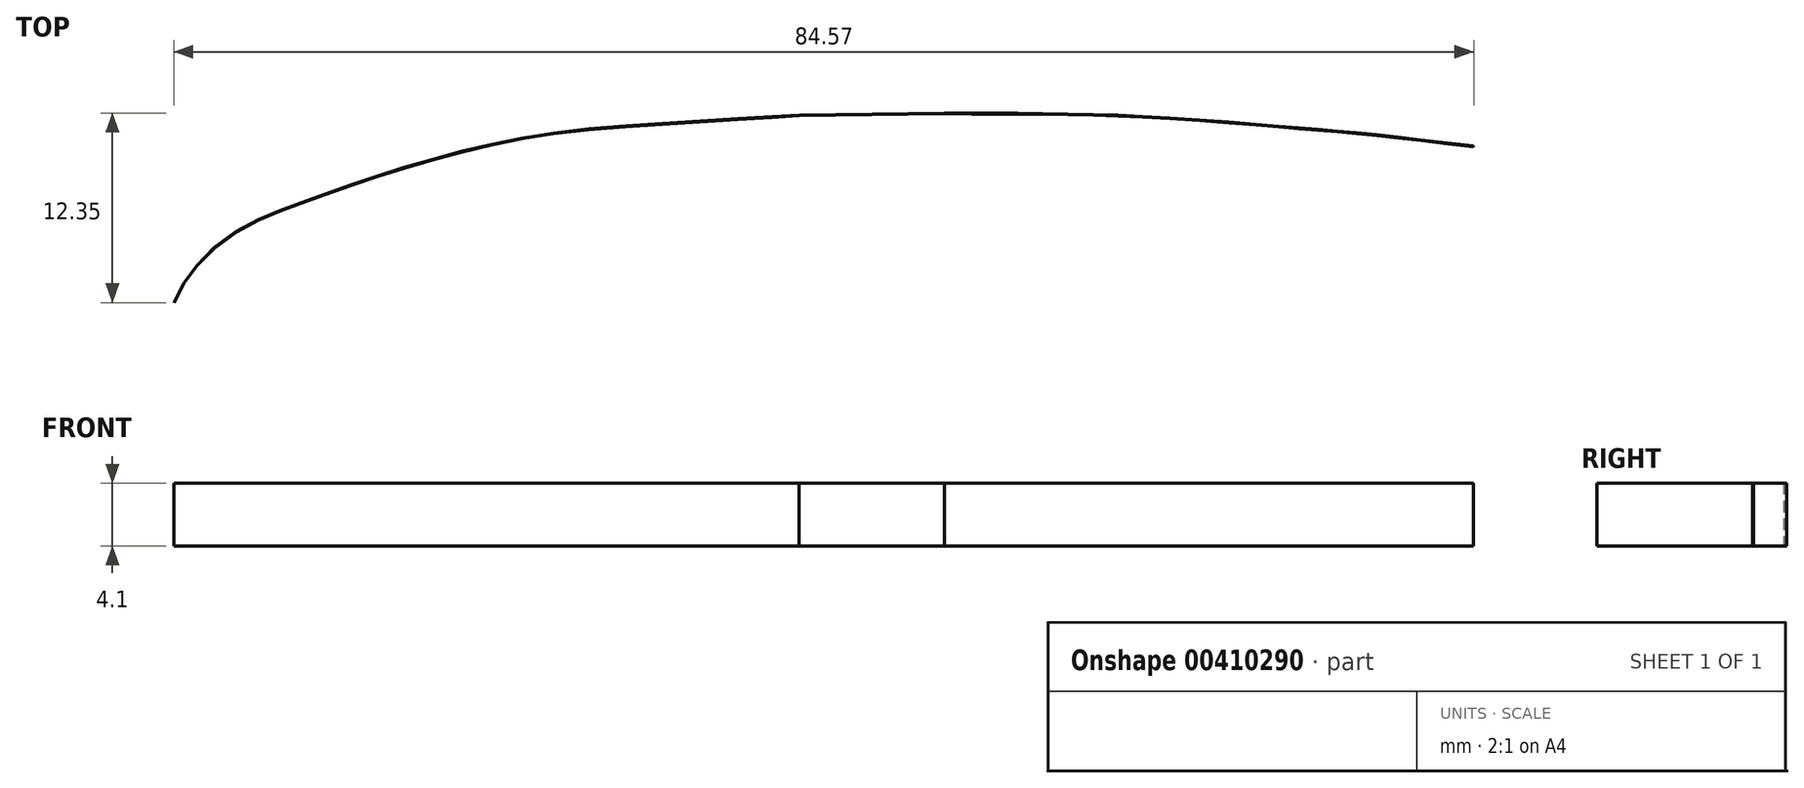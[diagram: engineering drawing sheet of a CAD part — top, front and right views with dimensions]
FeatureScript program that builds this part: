
annotation { "Feature Type Name" : "Feature", "Feature Type Description" : "" }
export const myFeature = defineFeature(function(context is Context, id is Id, definition is map)
    precondition{}
    {
        {
            var Q0;
            Q0=qCreatedBy(makeId("Top.planeOp"),FACE);
            var sketch = newSketch(context, id + "F0", { "sketchPlane" : qUnion([Q0])});
            skLineSegment(sketch, "E0", {"start": v(-49.1, -7.29) * mm, "end": v(-49.1, 15.91) * mm, "construction": true});
            skLineSegment(sketch, "E1", {"start": v(56.1, -3.3) * mm, "end": v(55.68, 15.32) * mm, "construction": true});
            skFitSpline(sketch, "E2.0", {"points": [v(-7.16, 11.34) * mm, v(-8.7, 11.24) * mm, v(-11.02, 11.1) * mm, v(-14.06, 10.9) * mm, v(-17.04, 10.72) * mm, v(-19.9, 10.52) * mm, v(-22.68, 10.23) * mm, v(-24.74, 9.92) * mm, v(-26.8, 9.52) * mm, v(-28.8, 9.06) * mm, v(-30.7, 8.56) * mm, v(-32.46, 8.05) * mm, v(-34.1, 7.54) * mm, v(-35.64, 7.03) * mm, v(-37.16, 6.5) * mm, v(-38.65, 5.98) * mm, v(-39.87, 5.53) * mm, v(-40.85, 5.16) * mm, v(-41.8, 4.78) * mm, v(-42.94, 4.26) * mm, v(-44.23, 3.5) * mm, v(-45.45, 2.52) * mm, v(-46.35, 1.6) * mm, v(-46.94, 0.82) * mm, v(-47.45, 0.03) * mm, v(-47.92, -0.97) * mm, v(-48.28, -2.27) * mm, v(-48.48, -3.72) * mm, v(-48.48, -4.98) * mm, v(-48.37, -6) * mm, v(-48.22, -6.76) * mm, v(-48, -7.52) * mm, v(-47.64, -8.53) * mm, v(-47.03, -9.76) * mm, v(-46.16, -11.04) * mm, v(-45.39, -11.86) * mm, v(-44.73, -12.42) * mm, v(-44.23, -12.82) * mm, v(-43.7, -13.19) * mm, v(-42.97, -13.66) * mm, v(-42.25, -14.07) * mm, v(-41.5, -14.41) * mm, v(-40.9, -14.62) * mm, v(-40.26, -14.8) * mm, v(-39.57, -14.92) * mm, v(-38.86, -14.99) * mm, v(-38.15, -15) * mm, v(-37.45, -14.98) * mm, v(-36.8, -14.88) * mm, v(-36.13, -14.74) * mm, v(-35.25, -14.49) * mm, v(-34.35, -14.16) * mm, v(-33.37, -13.82) * mm, v(-32.36, -13.48) * mm, v(-31.03, -13.06) * mm, v(-29.3, -12.61) * mm, v(-27.44, -12.24) * mm, v(-25.89, -12) * mm, v(-24.73, -11.82) * mm, v(-23.93, -11.7) * mm, v(-23.2, -11.58) * mm, v(-22.55, -11.46) * mm, v(-21.9, -11.35) * mm, v(-21.24, -11.25) * mm, v(-20.54, -11.16) * mm, v(-19.75, -11.07) * mm, v(-18.91, -11) * mm, v(-18.02, -10.93) * mm, v(-17.1, -10.87) * mm, v(-16.19, -10.82) * mm, v(-15.27, -10.79) * mm, v(-14.39, -10.76) * mm, v(-13.53, -10.75) * mm, v(-12.4, -10.76) * mm, v(-11.27, -10.79) * mm, v(-10.13, -10.85) * mm, v(-8.95, -10.94) * mm, v(-7.77, -11.05) * mm, v(-6.62, -11.18) * mm, v(-5.79, -11.27) * mm, v(-5, -11.36) * mm, v(-4.02, -11.47) * mm, v(-2.87, -11.6) * mm, v(-1.47, -11.7) * mm, v(0.14, -11.8) * mm, v(1.9, -11.88) * mm, v(3.11, -11.93) * mm, v(3.72, -11.95) * mm]});
            skFitSpline(sketch, "E2.1", {"points": [v(-7.21, 11.34) * mm, v(-4.05, 11.38) * mm, v(-0.89, 11.42) * mm, v(2.27, 11.46) * mm]});
            skFitSpline(sketch, "E2.2", {"points": [v(3.5, -11.97) * mm, v(4.13, -11.85) * mm, v(5.02, -11.8) * mm, v(6.1, -11.8) * mm, v(6.78, -11.8) * mm, v(7.33, -11.78) * mm, v(7.9, -11.75) * mm, v(8.66, -11.67) * mm, v(9.64, -11.54) * mm, v(10.65, -11.39) * mm, v(11.68, -11.2) * mm, v(13.05, -10.96) * mm, v(14.68, -10.67) * mm, v(16.31, -10.31) * mm, v(17.67, -9.95) * mm, v(18.73, -9.63) * mm, v(19.84, -9.26) * mm, v(20.96, -8.86) * mm, v(22.04, -8.45) * mm, v(23.06, -8.05) * mm, v(23.82, -7.74) * mm, v(24.36, -7.52) * mm, v(24.85, -7.31) * mm, v(25.4, -7.09) * mm, v(26.03, -6.86) * mm, v(26.7, -6.7) * mm, v(27.43, -6.6) * mm, v(28.16, -6.58) * mm, v(29.14, -6.62) * mm, v(30.06, -6.75) * mm, v(30.96, -6.99) * mm, v(31.86, -7.3) * mm, v(33.02, -7.83) * mm, v(34.24, -8.6) * mm, v(35.27, -9.38) * mm, v(36.04, -10.03) * mm, v(36.63, -10.6) * mm, v(37.06, -11.08) * mm, v(37.36, -11.44) * mm, v(37.63, -11.81) * mm, v(37.86, -12.2) * mm, v(38.04, -12.56) * mm, v(38.18, -12.89) * mm, v(38.3, -13.18) * mm, v(38.4, -13.42) * mm, v(38.5, -13.62) * mm, v(38.58, -13.76) * mm, v(38.65, -13.86) * mm, v(38.74, -13.97) * mm, v(38.87, -14.1) * mm, v(39.06, -14.28) * mm, v(39.35, -14.49) * mm, v(39.67, -14.68) * mm, v(40, -14.82) * mm, v(40.33, -14.93) * mm, v(40.73, -15.01) * mm, v(41.27, -15.03) * mm, v(41.9, -14.95) * mm, v(42.66, -14.76) * mm, v(43.56, -14.46) * mm, v(44.54, -14.08) * mm, v(45.57, -13.66) * mm, v(46.63, -13.22) * mm, v(47.52, -12.87) * mm, v(48.21, -12.61) * mm, v(48.89, -12.38) * mm, v(49.67, -12.12) * mm, v(50.52, -11.83) * mm, v(51.28, -11.52) * mm, v(51.84, -11.22) * mm, v(52.25, -10.94) * mm, v(52.65, -10.62) * mm, v(53.13, -10.13) * mm, v(53.66, -9.45) * mm, v(54.13, -8.69) * mm, v(54.44, -8.02) * mm, v(54.64, -7.48) * mm, v(54.81, -6.94) * mm, v(54.96, -6.25) * mm, v(55.06, -5.42) * mm, v(55.1, -4.58) * mm, v(55.1, -3.75) * mm, v(55.1, -2.92) * mm, v(55.05, -1.92) * mm, v(54.94, -1.02) * mm, v(54.7, -0.16) * mm, v(54.41, 0.5) * mm, v(54.05, 1.2) * mm, v(53.47, 2.12) * mm, v(52.63, 3.23) * mm, v(51.72, 4.23) * mm, v(51, 4.94) * mm, v(50.47, 5.43) * mm, v(49.97, 5.86) * mm, v(49.48, 6.25) * mm, v(48.96, 6.6) * mm, v(48.37, 6.96) * mm, v(47.68, 7.3) * mm, v(46.7, 7.73) * mm, v(45.37, 8.19) * mm, v(44.14, 8.44) * mm, v(43.04, 8.6) * mm, v(42.12, 8.7) * mm, v(41.07, 8.8) * mm, v(39.88, 8.94) * mm, v(38.56, 9.09) * mm, v(36.7, 9.31) * mm, v(34.75, 9.54) * mm, v(32.85, 9.77) * mm, v(31.48, 9.92) * mm, v(30.22, 10.06) * mm, v(29.07, 10.17) * mm, v(28, 10.27) * mm, v(26.96, 10.36) * mm, v(25.92, 10.45) * mm, v(24.85, 10.53) * mm, v(23.72, 10.63) * mm, v(22.1, 10.77) * mm, v(19.87, 10.95) * mm, v(17.38, 11.12) * mm, v(15.24, 11.24) * mm, v(13.55, 11.31) * mm, v(11.79, 11.37) * mm, v(9.97, 11.4) * mm, v(8.2, 11.43) * mm, v(6.5, 11.45) * mm, v(5, 11.45) * mm, v(3.72, 11.45) * mm, v(2.92, 11.46) * mm, v(2.47, 11.46) * mm, v(2.3, 11.46) * mm, v(2.24, 11.46) * mm]});
            skArc(sketch, "E3", {"start": v(9.18, 8.55) * mm, "mid": v(8.26, 9.24) * mm, "end": v(7.1, 9.31) * mm});
            skArc(sketch, "E4", {"start": v(36.35, 6.78) * mm, "mid": v(35.45, 7.49) * mm, "end": v(34.3, 7.58) * mm});
            skFitSpline(sketch, "E5.0", {"points": [v(-7.18, 11.29) * mm, v(-8.73, 11.2) * mm, v(-11.04, 11.05) * mm, v(-14.07, 10.86) * mm, v(-17.06, 10.67) * mm, v(-19.92, 10.47) * mm, v(-22.7, 10.18) * mm, v(-24.75, 9.87) * mm, v(-26.81, 9.47) * mm, v(-28.81, 9.01) * mm, v(-30.72, 8.5) * mm, v(-32.48, 8) * mm, v(-34.11, 7.5) * mm, v(-35.66, 6.98) * mm, v(-37.18, 6.46) * mm, v(-38.67, 5.93) * mm, v(-39.9, 5.48) * mm, v(-40.87, 5.12) * mm, v(-41.82, 4.74) * mm, v(-42.96, 4.21) * mm, v(-44.25, 3.45) * mm, v(-45.47, 2.47) * mm, v(-46.37, 1.54) * mm, v(-46.96, 0.77) * mm, v(-47.47, -0.02) * mm, v(-47.94, -1.02) * mm, v(-48.3, -2.32) * mm, v(-48.5, -3.76) * mm, v(-48.5, -5.02) * mm, v(-48.39, -6.05) * mm, v(-48.24, -6.8) * mm, v(-48.03, -7.57) * mm, v(-47.65, -8.58) * mm, v(-47.05, -9.8) * mm, v(-46.17, -11.09) * mm, v(-45.4, -11.9) * mm, v(-44.75, -12.47) * mm, v(-44.25, -12.87) * mm, v(-43.72, -13.24) * mm, v(-43, -13.71) * mm, v(-42.27, -14.12) * mm, v(-41.52, -14.46) * mm, v(-40.92, -14.67) * mm, v(-40.28, -14.84) * mm, v(-39.59, -14.97) * mm, v(-38.88, -15.04) * mm, v(-38.17, -15.06) * mm, v(-37.47, -15.02) * mm, v(-36.8, -14.93) * mm, v(-36.15, -14.79) * mm, v(-35.27, -14.54) * mm, v(-34.36, -14.21) * mm, v(-33.39, -13.87) * mm, v(-32.38, -13.53) * mm, v(-31.05, -13.11) * mm, v(-29.33, -12.66) * mm, v(-27.46, -12.3) * mm, v(-25.9, -12.04) * mm, v(-24.75, -11.87) * mm, v(-23.94, -11.74) * mm, v(-23.23, -11.62) * mm, v(-22.56, -11.51) * mm, v(-21.92, -11.4) * mm, v(-21.26, -11.3) * mm, v(-20.56, -11.2) * mm, v(-19.77, -11.12) * mm, v(-18.93, -11.04) * mm, v(-18.04, -10.97) * mm, v(-17.13, -10.92) * mm, v(-16.2, -10.87) * mm, v(-15.3, -10.84) * mm, v(-14.4, -10.81) * mm, v(-13.55, -10.8) * mm, v(-12.41, -10.8) * mm, v(-11.3, -10.84) * mm, v(-10.15, -10.9) * mm, v(-8.97, -10.99) * mm, v(-7.79, -11.1) * mm, v(-6.64, -11.23) * mm, v(-5.8, -11.32) * mm, v(-5.02, -11.4) * mm, v(-4.04, -11.52) * mm, v(-2.9, -11.64) * mm, v(-1.49, -11.76) * mm, v(0.12, -11.85) * mm, v(1.88, -11.93) * mm, v(3.1, -11.98) * mm, v(3.7, -12) * mm]});
            skFitSpline(sketch, "E5.1", {"points": [v(-7.23, 11.29) * mm, v(-4.07, 11.33) * mm, v(-0.9, 11.37) * mm, v(2.26, 11.41) * mm]});
            skFitSpline(sketch, "E5.2", {"points": [v(3.48, -12.02) * mm, v(4.11, -11.9) * mm, v(5, -11.85) * mm, v(6.09, -11.85) * mm, v(6.76, -11.85) * mm, v(7.3, -11.83) * mm, v(7.88, -11.8) * mm, v(8.65, -11.72) * mm, v(9.62, -11.6) * mm, v(10.63, -11.43) * mm, v(11.66, -11.26) * mm, v(13.03, -11.01) * mm, v(14.67, -10.72) * mm, v(16.3, -10.36) * mm, v(17.65, -10) * mm, v(18.7, -9.68) * mm, v(19.82, -9.3) * mm, v(20.94, -8.9) * mm, v(22.02, -8.5) * mm, v(23.04, -8.1) * mm, v(23.8, -7.79) * mm, v(24.34, -7.57) * mm, v(24.83, -7.36) * mm, v(25.37, -7.14) * mm, v(26.01, -6.91) * mm, v(26.69, -6.74) * mm, v(27.41, -6.65) * mm, v(28.14, -6.63) * mm, v(29.12, -6.67) * mm, v(30.04, -6.8) * mm, v(30.94, -7.04) * mm, v(31.84, -7.35) * mm, v(33, -7.88) * mm, v(34.22, -8.65) * mm, v(35.25, -9.43) * mm, v(36.02, -10.08) * mm, v(36.61, -10.65) * mm, v(37.04, -11.13) * mm, v(37.34, -11.5) * mm, v(37.61, -11.86) * mm, v(37.84, -12.25) * mm, v(38.02, -12.6) * mm, v(38.16, -12.94) * mm, v(38.28, -13.22) * mm, v(38.38, -13.47) * mm, v(38.48, -13.67) * mm, v(38.56, -13.8) * mm, v(38.63, -13.9) * mm, v(38.72, -14.02) * mm, v(38.85, -14.16) * mm, v(39.04, -14.33) * mm, v(39.33, -14.54) * mm, v(39.65, -14.73) * mm, v(39.98, -14.87) * mm, v(40.3, -14.98) * mm, v(40.71, -15.06) * mm, v(41.25, -15.08) * mm, v(41.88, -15) * mm, v(42.64, -14.81) * mm, v(43.54, -14.51) * mm, v(44.52, -14.13) * mm, v(45.55, -13.71) * mm, v(46.62, -13.27) * mm, v(47.5, -12.92) * mm, v(48.2, -12.66) * mm, v(48.87, -12.43) * mm, v(49.65, -12.17) * mm, v(50.5, -11.88) * mm, v(51.26, -11.57) * mm, v(51.82, -11.27) * mm, v(52.23, -10.99) * mm, v(52.63, -10.67) * mm, v(53.11, -10.18) * mm, v(53.64, -9.5) * mm, v(54.1, -8.74) * mm, v(54.42, -8.07) * mm, v(54.63, -7.53) * mm, v(54.8, -6.99) * mm, v(54.94, -6.3) * mm, v(55.04, -5.47) * mm, v(55.09, -4.63) * mm, v(55.09, -3.8) * mm, v(55.07, -2.97) * mm, v(55.04, -1.97) * mm, v(54.92, -1.07) * mm, v(54.67, -0.21) * mm, v(54.4, 0.46) * mm, v(54.03, 1.15) * mm, v(53.45, 2.07) * mm, v(52.6, 3.18) * mm, v(51.7, 4.18) * mm, v(50.98, 4.89) * mm, v(50.45, 5.38) * mm, v(49.95, 5.82) * mm, v(49.46, 6.2) * mm, v(48.94, 6.56) * mm, v(48.35, 6.9) * mm, v(47.66, 7.25) * mm, v(46.67, 7.68) * mm, v(45.35, 8.14) * mm, v(44.12, 8.4) * mm, v(43.02, 8.55) * mm, v(42.1, 8.65) * mm, v(41.06, 8.76) * mm, v(39.86, 8.89) * mm, v(38.54, 9.04) * mm, v(36.68, 9.26) * mm, v(34.73, 9.5) * mm, v(32.83, 9.72) * mm, v(31.46, 9.87) * mm, v(30.2, 10) * mm, v(29.06, 10.12) * mm, v(27.98, 10.22) * mm, v(26.94, 10.31) * mm, v(25.9, 10.4) * mm, v(24.84, 10.48) * mm, v(23.7, 10.58) * mm, v(22.08, 10.72) * mm, v(19.85, 10.9) * mm, v(17.36, 11.07) * mm, v(15.22, 11.19) * mm, v(13.53, 11.26) * mm, v(11.77, 11.32) * mm, v(9.96, 11.36) * mm, v(8.17, 11.38) * mm, v(6.49, 11.4) * mm, v(4.97, 11.4) * mm, v(3.7, 11.4) * mm, v(2.9, 11.4) * mm, v(2.45, 11.4) * mm, v(2.29, 11.41) * mm, v(2.22, 11.41) * mm]});
            skCircle(sketch, "E6", {"center": v(-44.34, -5.92) * mm, "radius": 2.1 * mm});
            skCircle(sketch, "E7", {"center": v(-19.07, 6.55) * mm, "radius": 2.1 * mm});
            skArc(sketch, "E8", {"start": v(9.14, 8.55) * mm, "mid": v(8.25, 9.21) * mm, "end": v(7.15, 9.3) * mm});
            skArc(sketch, "E9", {"start": v(9.14, 8.55) * mm, "mid": v(9.22, 8.59) * mm, "end": v(9.3, 8.63) * mm});
            skFitSpline(sketch, "E10", {"points": [v(-15.32, 8.96) * mm, v(7.15, 9.3) * mm, v(17.25, 3.77) * mm], "startDerivative": vector(42.73, 4.67) * mm, "endDerivative": vector(21.23, -16.2) * mm});
            skFitSpline(sketch, "E11.trimOffspring", {"points": [v(-15.32, 8.96) * mm, v(7.15, 9.3) * mm, v(17.25, 3.77) * mm], "startDerivative": vector(42.73, 4.67) * mm, "endDerivative": vector(21.23, -16.2) * mm});
            skArc(sketch, "E12.trimOffspring", {"start": v(-21.7, 4.94) * mm, "mid": v(-33.14, 5.53) * mm, "end": v(-42.33, -1.34) * mm});
            skArc(sketch, "E13", {"start": v(-21.7, 4.94) * mm, "mid": v(-20.44, 4.08) * mm, "end": v(-18.95, 3.77) * mm});
            skFitSpline(sketch, "E14", {"points": [v(-15.32, 8.96) * mm, v(-16.43, 8.6) * mm], "startDerivative": vector(-1.12, -0.35) * mm, "endDerivative": vector(-1.12, -0.35) * mm});
            skArc(sketch, "E15", {"start": v(-21.7, 4.94) * mm, "mid": v(-17.37, 4.34) * mm, "end": v(-16.43, 8.6) * mm});
            skArc(sketch, "E16", {"start": v(-48.41, -5.77) * mm, "mid": v(-41.77, -8.5) * mm, "end": v(-42.33, -1.34) * mm});
            skArc(sketch, "E17", {"start": v(36.35, 6.78) * mm, "mid": v(36.88, 8) * mm, "end": v(36.65, 9.32) * mm});
            skFitSpline(sketch, "E18", {"points": [v(9.14, 8.55) * mm, v(34.3, 7.58) * mm, v(36.26, 4.92) * mm], "startDerivative": vector(44.16, 1.89) * mm, "endDerivative": vector(3.78, -11.19) * mm});
            skSolve(sketch);
        }
        {
            var Q0;
            {var subQ10=sQuery(id+"F0.wireOp",EDGE,"E2.1");Q0=makeQuery(id+"F0.imprint","IMPRINT",FACE,{"disambiguationData":[TD([[makeQuery(id+"F0.imprint","IMPRINT",EDGE,{"derivedFrom":subQ10}),-1.0]])]});}
            extrude(context, id + "F1", {"entities" : qUnion([Q0]), "depth" : 4.1 * mm});
        }
    });
